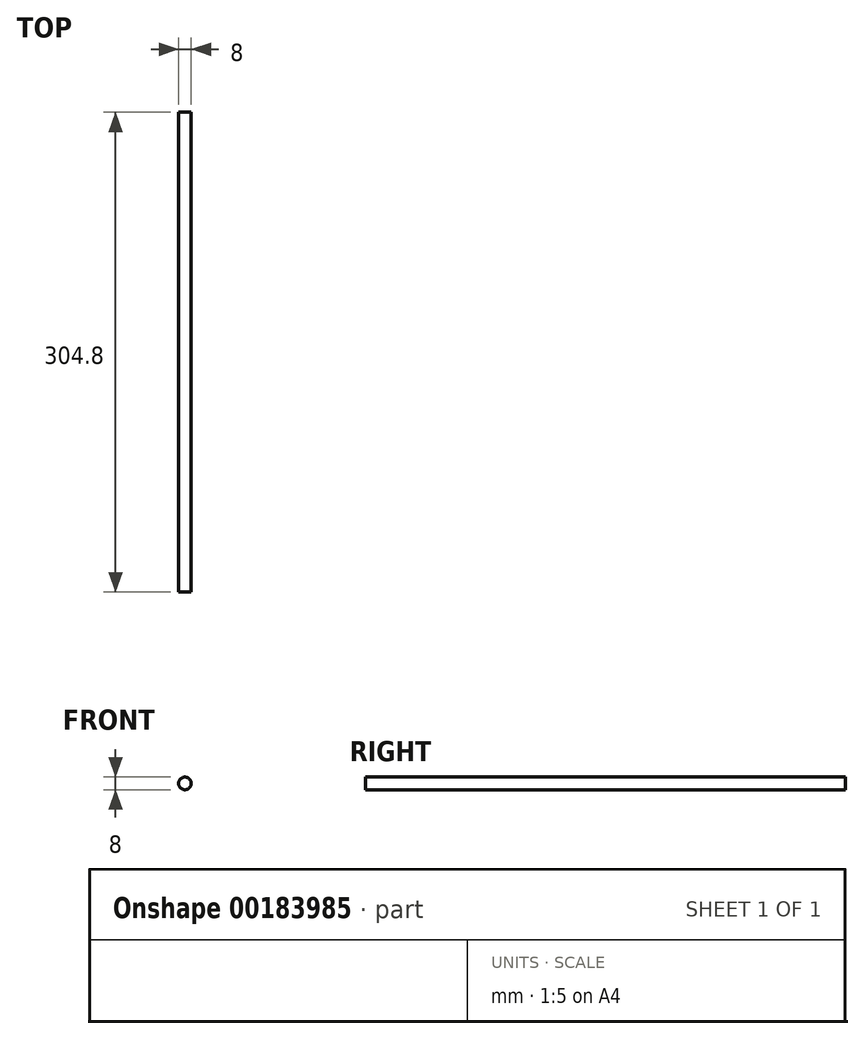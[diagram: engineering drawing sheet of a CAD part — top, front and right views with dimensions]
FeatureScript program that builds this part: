
annotation { "Feature Type Name" : "Feature", "Feature Type Description" : "" }
export const myFeature = defineFeature(function(context is Context, id is Id, definition is map)
    precondition{}
    {
        {
            var Q0;
            Q0=qCreatedBy(makeId("Front.planeOp"),FACE);
            var sketch = newSketch(context, id + "F0", { "sketchPlane" : qUnion([Q0])});
            skCircle(sketch, "E0", {"center": v(0, 0) * mm, "radius": 4 * mm});
            skSolve(sketch);
        }
        {
            var Q0;
            Q0=makeQuery(id+"F0.imprint","IMPRINT",FACE,{"disambiguationData":[TD([[makeQuery(id+"F0.imprint","IMPRINT",EDGE,{"derivedFrom":sQuery(id+"F0.wireOp",EDGE,"E0")}),1.0]])]});
            extrude(context, id + "F1", {"entities" : qUnion([Q0]), "depth" : 304.8 * mm});
        }
    });
